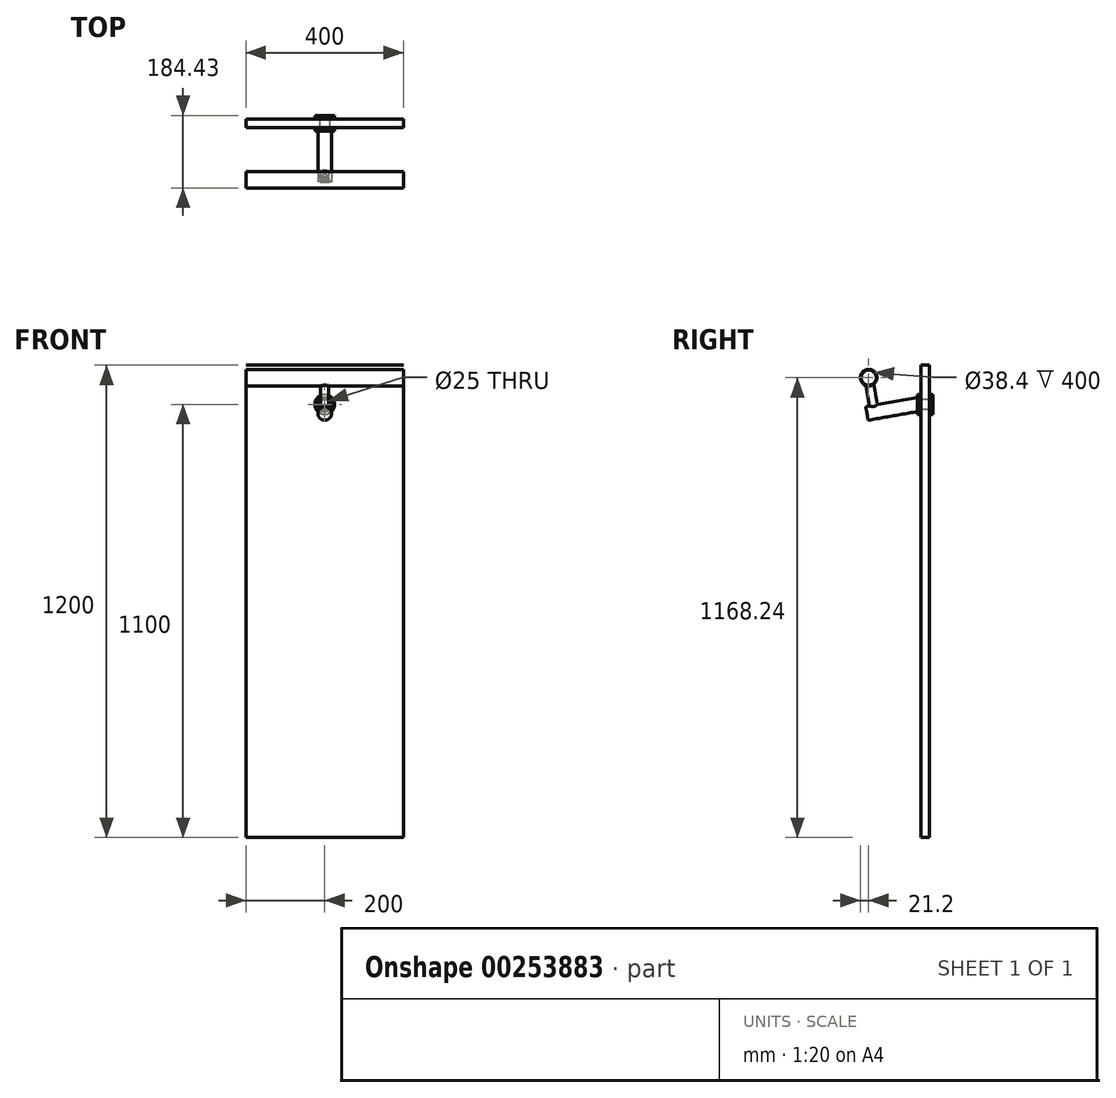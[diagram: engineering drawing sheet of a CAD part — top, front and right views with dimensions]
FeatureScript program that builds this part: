
annotation { "Feature Type Name" : "Feature", "Feature Type Description" : "" }
export const myFeature = defineFeature(function(context is Context, id is Id, definition is map)
    precondition{}
    {
        {
            var Q0;
            Q0=qCreatedBy(makeId("Front.planeOp"),FACE);
            var sketch = newSketch(context, id + "F0", { "sketchPlane" : qUnion([Q0])});
            skLineSegment(sketch, "E0.bottom", {"start": v(0, 0) * mm, "end": v(400, 0) * mm});
            skLineSegment(sketch, "E0.top", {"start": v(0, 1200) * mm, "end": v(400, 1200) * mm});
            skLineSegment(sketch, "E0.left", {"start": v(0, 0) * mm, "end": v(0, 1200) * mm});
            skLineSegment(sketch, "E0.right", {"start": v(400, 0) * mm, "end": v(400, 1200) * mm});
            skSolve(sketch);
        }
        {
            var Q0;
            Q0=makeQuery(id+"F0.imprint","IMPRINT",FACE,{"disambiguationData":[TD([[makeQuery(id+"F0.imprint","IMPRINT",EDGE,{"derivedFrom":sQuery(id+"F0.wireOp",EDGE,"E0.bottom")}),1.0]])]});
            extrude(context, id + "F1", {"entities" : qUnion([Q0]), "endBound" : BoundingType.SYMMETRIC, "depth" : 21.5 * mm});
        }
        {
            var Q0;
            Q0=makeQuery(id+"F1.opExtrude","CAP_FACE",FACE,{"disambiguationData":[OSD([sQuery(id+"F0.wireOp",EDGE,"E0.bottom"),sQuery(id+"F0.wireOp",EDGE,"E0.top"),sQuery(id+"F0.wireOp",EDGE,"E0.left"),sQuery(id+"F0.wireOp",EDGE,"E0.right")])],"isStart":false});
            var sketch = newSketch(context, id + "F2", { "sketchPlane" : qUnion([Q0])});
            skPoint(sketch, "E1", {"position": v(200, 1100) * mm});
            skPoint(sketch, "E1.positionSnap0", {"position": v(200, 1200) * mm});
            skSolve(sketch);
        }
        {
            var Q0;
            Q0=sQuery(id+"F2.wireOp",VERTEX,"E1");
            var Q1;
            Q1=makeQuery(id+"F1.opExtrude","SWEPT_BODY",BODY,{"disambiguationData":[OSD([sQuery(id+"F0.wireOp",EDGE,"E0.bottom"),sQuery(id+"F0.wireOp",EDGE,"E0.top"),sQuery(id+"F0.wireOp",EDGE,"E0.left"),sQuery(id+"F0.wireOp",EDGE,"E0.right")])]});
            hole(context, id + "F3", {"style" : HoleStyle.SIMPLE, "endStyle" : HoleEndStyle.THROUGH, "holeDiameter" : 25 * mm, "tappedDepth" : 12 * mm, "tapClearance" : 3, "locations" : qUnion([Q0]), "scope" : qUnion([Q1])});
        }
        {
            var Q0;
            Q0=makeQuery(id+"F1.opExtrude","CAP_FACE",FACE,{"disambiguationData":[OSD([sQuery(id+"F0.wireOp",EDGE,"E0.bottom"),sQuery(id+"F0.wireOp",EDGE,"E0.top"),sQuery(id+"F0.wireOp",EDGE,"E0.left"),sQuery(id+"F0.wireOp",EDGE,"E0.right")])],"isStart":true});
            cPlane(context, id + "F4", {"entities" : qUnion([Q0]), "cplaneType" : CPlaneType.OFFSET, "offset" : 1 * mm, "width" : 150 * mm, "height" : 150 * mm});
        }
        {
            var Q0;
            Q0=qCreatedBy(id+"F4.planeOp",FACE);
            var sketch = newSketch(context, id + "F5", { "sketchPlane" : qUnion([Q0])});
            skCircle(sketch, "E2", {"center": v(-200, 1100) * mm, "radius": 25 * mm});
            skSolve(sketch);
        }
        {
            var Q0;
            Q0=makeQuery(id+"F5.imprint","IMPRINT",FACE,{"disambiguationData":[TD([[makeQuery(id+"F5.imprint","IMPRINT",EDGE,{"derivedFrom":sQuery(id+"F5.wireOp",EDGE,"E2")}),1.0]])]});
            extrude(context, id + "F6", {"entities" : qUnion([Q0]), "depth" : 8 * mm});
        }
        {
            var Q0;
            Q0=makeQuery(id+"F1.opExtrude","CAP_FACE",FACE,{"disambiguationData":[OSD([sQuery(id+"F0.wireOp",EDGE,"E0.bottom"),sQuery(id+"F0.wireOp",EDGE,"E0.top"),sQuery(id+"F0.wireOp",EDGE,"E0.left"),sQuery(id+"F0.wireOp",EDGE,"E0.right")])],"isStart":false});
            cPlane(context, id + "F7", {"entities" : qUnion([Q0]), "cplaneType" : CPlaneType.OFFSET, "offset" : 1 * mm, "width" : 150 * mm, "height" : 150 * mm});
        }
        {
            var Q0;
            Q0=qCreatedBy(id+"F7.planeOp",FACE);
            var sketch = newSketch(context, id + "F8", { "sketchPlane" : qUnion([Q0])});
            skCircle(sketch, "E3", {"center": v(200, 1100) * mm, "radius": 25 * mm});
            skSolve(sketch);
        }
        {
            var Q0;
            Q0=makeQuery(id+"F8.imprint","IMPRINT",FACE,{"disambiguationData":[TD([[makeQuery(id+"F8.imprint","IMPRINT",EDGE,{"derivedFrom":sQuery(id+"F8.wireOp",EDGE,"E3")}),1.0]])]});
            extrude(context, id + "F9", {"entities" : qUnion([Q0]), "depth" : 8 * mm});
        }
        {
            var Q0;
            Q0=makeQuery(id+"F1.opExtrude","SWEPT_FACE",FACE,{"disambiguationData":[OSD([sQuery(id+"F0.wireOp",EDGE,"E0.left")])]});
            var Q1;
            Q1=makeQuery(id+"F1.opExtrude","SWEPT_FACE",FACE,{"disambiguationData":[OSD([sQuery(id+"F0.wireOp",EDGE,"E0.right")])]});
            cPlane(context, id + "F10", {"entities" : qUnion([Q0, Q1]), "cplaneType" : CPlaneType.MID_PLANE, "offset" : 25 * mm, "width" : 150 * mm, "height" : 150 * mm});
        }
        {
            var Q0;
            Q0=makeQuery(id+"F9.opExtrude","CAP_FACE",FACE,{"disambiguationData":[OSD([sQuery(id+"F8.wireOp",EDGE,"E3")])],"isStart":false});
            var sketch = newSketch(context, id + "F11", { "sketchPlane" : qUnion([Q0])});
            skPoint(sketch, "E4", {"position": v(200, 1100) * mm});
            skSolve(sketch);
        }
        {
            var Q0;
            Q0=qCreatedBy(id+"F10.planeOp",FACE);
            var sketch = newSketch(context, id + "F12", { "sketchPlane" : qUnion([Q0])});
            skLineSegment(sketch, "E5", {"start": v(19.75, 1100) * mm, "end": v(147.78, 1077.43) * mm});
            skSolve(sketch);
        }
        {
            var Q0;
            Q0=sQuery(id+"F12.wireOp",VERTEX,"E5.end");
            var Q1;
            Q1=sQuery(id+"F12.wireOp",EDGE,"E5");
            cPlane(context, id + "F13", {"entities" : qUnion([Q0, Q1]), "cplaneType" : CPlaneType.LINE_POINT, "offset" : 25 * mm, "width" : 150 * mm, "height" : 150 * mm});
        }
        {
            var Q0;
            Q0=qCreatedBy(id+"F13.planeOp",FACE);
            var sketch = newSketch(context, id + "F14", { "sketchPlane" : qUnion([Q0])});
            skCircle(sketch, "E6", {"center": v(200, 1086.72) * mm, "radius": 17.5 * mm});
            skSolve(sketch);
        }
        {
            var Q0;
            Q0=makeQuery(id+"F14.imprint","IMPRINT",FACE,{"disambiguationData":[TD([[makeQuery(id+"F14.imprint","IMPRINT",EDGE,{"derivedFrom":sQuery(id+"F14.wireOp",EDGE,"E6")}),1.0]])]});
            var Q1;
            Q1=makeQuery(id+"F9.opExtrude","CAP_FACE",FACE,{"disambiguationData":[OSD([sQuery(id+"F8.wireOp",EDGE,"E3")])],"isStart":false});
            extrude(context, id + "F15", {"entities" : qUnion([Q0, Q1]), "endBound" : BoundingType.UP_TO_NEXT, "oppositeDirection" : true, "depth" : 25 * mm});
        }
        {
            var Q0;
            Q0=qCreatedBy(id+"F10.planeOp",FACE);
            var sketch = newSketch(context, id + "F16", { "sketchPlane" : qUnion([Q0])});
            skLineSegment(sketch, "E7", {"start": v(128.72, 1084.53) * mm, "end": v(140.23, 1149.84) * mm});
            skLineSegment(sketch, "E8", {"start": v(140.23, 1149.84) * mm, "end": v(130.39, 1151.57) * mm});
            skLineSegment(sketch, "E9", {"start": v(130.39, 1151.57) * mm, "end": v(118.87, 1086.27) * mm});
            skLineSegment(sketch, "E10", {"start": v(118.87, 1086.27) * mm, "end": v(128.72, 1084.53) * mm});
            skLineSegment(sketch, "E11", {"start": v(128.72, 1084.53) * mm, "end": v(138.57, 1082.8) * mm});
            skLineSegment(sketch, "E12", {"start": v(138.57, 1082.8) * mm, "end": v(150.08, 1148.1) * mm});
            skLineSegment(sketch, "E13", {"start": v(150.08, 1148.1) * mm, "end": v(140.23, 1149.84) * mm});
            skSolve(sketch);
        }
        {
            var Q0;
            Q0=makeQuery(id+"F16.imprint","IMPRINT",FACE,{"disambiguationData":[TD([[makeQuery(id+"F16.imprint","IMPRINT",EDGE,{"derivedFrom":sQuery(id+"F16.wireOp",EDGE,"E7")}),1.0]])]});
            var Q1;
            Q1=sQuery(id+"F16.wireOp",EDGE,"E7");
            revolve(context, id + "F17", {"operationType" : NewBodyOperationType.ADD, "entities" : qUnion([Q0]), "axis" : qUnion([Q1]), "revolveType" : RevolveType.FULL});
        }
        {
            var Q0;
            Q0=qCreatedBy(id+"F10.planeOp",FACE);
            var sketch = newSketch(context, id + "F18", { "sketchPlane" : qUnion([Q0])});
            skArc(sketch, "E14", {"start": v(130.39, 1151.57) * mm, "mid": v(139.8, 1147.37) * mm, "end": v(150.08, 1148.1) * mm});
            skSolve(sketch);
        }
        {
            var Q0;
            Q0=qCreatedBy(id+"F10.planeOp",FACE);
            var sketch = newSketch(context, id + "F19", { "sketchPlane" : qUnion([Q0])});
            skCircle(sketch, "E15", {"center": v(143.48, 1168.24) * mm, "radius": 21.2 * mm});
            skCircle(sketch, "E16.0", {"center": v(143.48, 1168.24) * mm, "radius": 19.2 * mm});
            skSolve(sketch);
        }
        {
            var Q0;
            Q0=makeQuery(id+"F19.imprint","IMPRINT",FACE,{"disambiguationData":[TD([[makeQuery(id+"F19.imprint","IMPRINT",EDGE,{"derivedFrom":sQuery(id+"F19.wireOp",EDGE,"E15")}),1.0]])]});
            extrude(context, id + "F20", {"entities" : qUnion([Q0]), "operationType" : NewBodyOperationType.ADD, "endBound" : BoundingType.SYMMETRIC, "depth" : 400 * mm});
        }
    });
